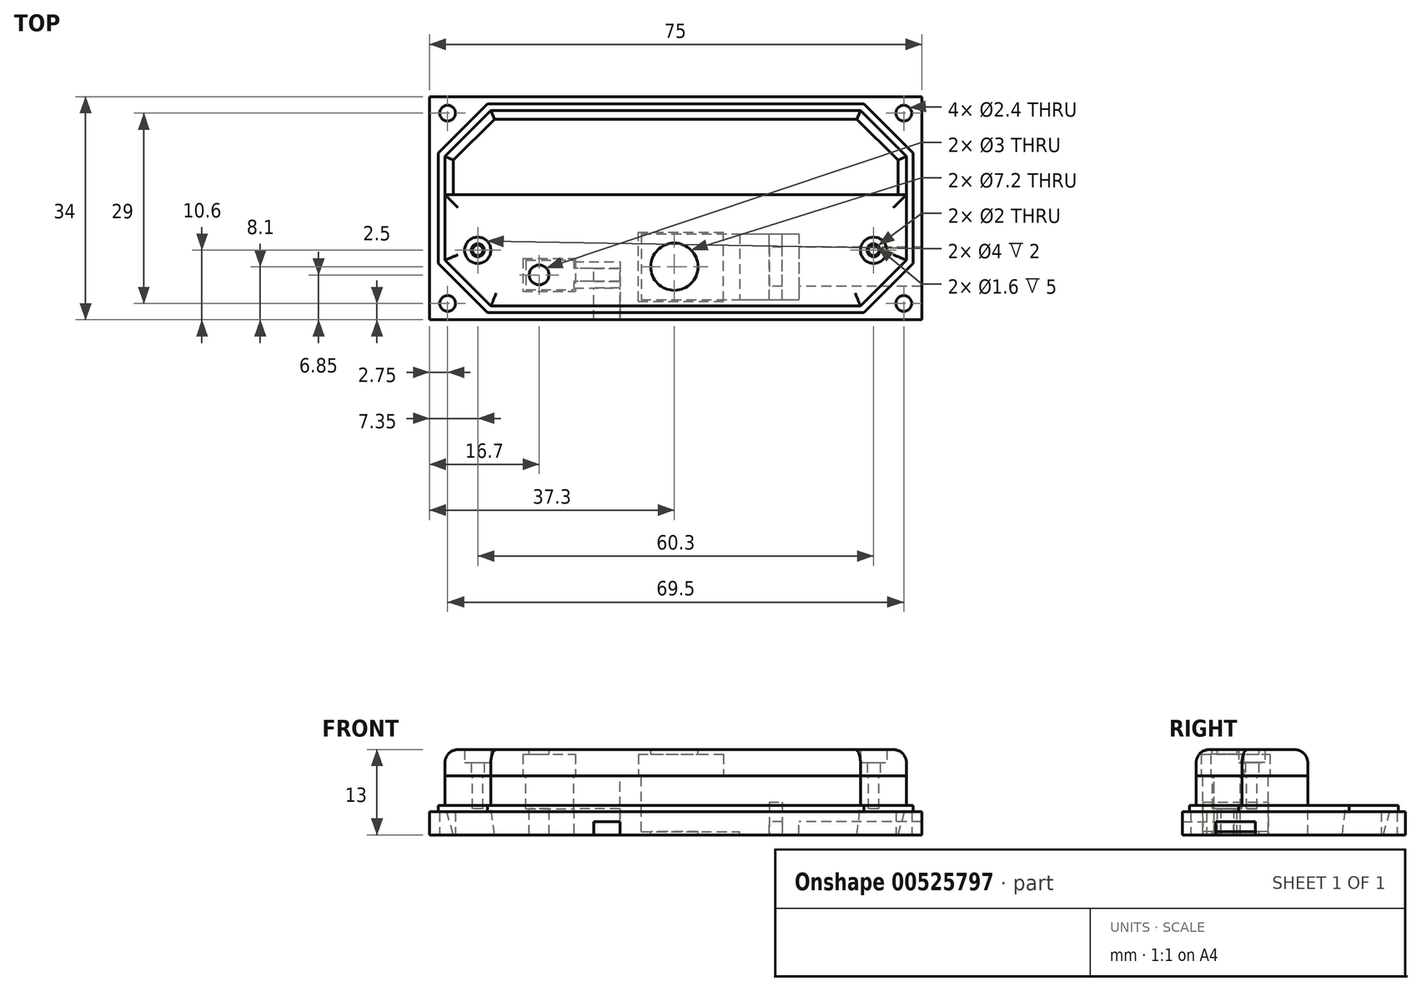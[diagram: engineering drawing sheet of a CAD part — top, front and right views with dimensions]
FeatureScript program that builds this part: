
annotation { "Feature Type Name" : "Feature", "Feature Type Description" : "" }
export const myFeature = defineFeature(function(context is Context, id is Id, definition is map)
    precondition{}
    {
        {
            var Q0;
            Q0=qCreatedBy(makeId("Top.planeOp"),FACE);
            var sketch = newSketch(context, id + "F0", { "sketchPlane" : qUnion([Q0])});
            skLineSegment(sketch, "E0.bottom", {"start": v(37.5, -17) * mm, "end": v(-37.5, -17) * mm});
            skLineSegment(sketch, "E0.top", {"start": v(37.5, 17) * mm, "end": v(-37.5, 17) * mm});
            skLineSegment(sketch, "E0.left", {"start": v(37.5, -17) * mm, "end": v(37.5, 17) * mm});
            skLineSegment(sketch, "E0.right", {"start": v(-37.5, -17) * mm, "end": v(-37.5, 17) * mm});
            skPoint(sketch, "E0.middle", {"position": v(0, 0) * mm});
            skLineSegment(sketch, "E1.bottom", {"start": v(-28.65, 15.9) * mm, "end": v(28.65, 15.9) * mm, "construction": true});
            skLineSegment(sketch, "E1.top", {"start": v(-28.65, -15.9) * mm, "end": v(28.65, -15.9) * mm, "construction": true});
            skLineSegment(sketch, "E1.left", {"start": v(-36.15, 8.4) * mm, "end": v(-36.15, -8.4) * mm, "construction": true});
            skLineSegment(sketch, "E1.right", {"start": v(36.15, 8.4) * mm, "end": v(36.15, -8.4) * mm, "construction": true});
            skLineSegment(sketch, "E2", {"start": v(-36.15, 8.4) * mm, "end": v(-28.65, 15.9) * mm, "construction": true});
            skLineSegment(sketch, "E3", {"start": v(28.65, 15.9) * mm, "end": v(36.15, 8.4) * mm, "construction": true});
            skLineSegment(sketch, "E4", {"start": v(36.15, -8.4) * mm, "end": v(28.65, -15.9) * mm, "construction": true});
            skLineSegment(sketch, "E5", {"start": v(-36.15, -8.4) * mm, "end": v(-28.65, -15.9) * mm, "construction": true});
            skCircle(sketch, "E6", {"center": v(-34.75, 14.5) * mm, "radius": 1.2 * mm});
            skCircle(sketch, "E7", {"center": v(34.75, 14.5) * mm, "radius": 1.2 * mm});
            skCircle(sketch, "E8", {"center": v(-34.75, -14.5) * mm, "radius": 1.2 * mm});
            skCircle(sketch, "E9", {"center": v(34.75, -14.5) * mm, "radius": 1.2 * mm});
            skLineSegment(sketch, "E10", {"start": v(0, -47.1) * mm, "end": v(0, -78.86) * mm, "construction": true});
            skSolve(sketch);
        }
        {
            var Q0;
            Q0=qSketchRegion(id+"F0",true);
            extrude(context, id + "F1", {"entities" : qUnion([Q0]), "depth" : 3.5 * mm});
        }
        {
            var Q0;
            Q0=makeQuery(id+"F1.opExtrude","CAP_FACE",FACE,{"disambiguationData":[OSD([sQuery(id+"F0.wireOp",EDGE,"E0.bottom"),sQuery(id+"F0.wireOp",EDGE,"E0.top"),sQuery(id+"F0.wireOp",EDGE,"E0.left"),sQuery(id+"F0.wireOp",EDGE,"E0.right"),sQuery(id+"F0.wireOp",EDGE,"E6"),sQuery(id+"F0.wireOp",EDGE,"E7"),sQuery(id+"F0.wireOp",EDGE,"E8"),sQuery(id+"F0.wireOp",EDGE,"E9")])],"isStart":false});
            var sketch = newSketch(context, id + "F2", { "sketchPlane" : qUnion([Q0])});
            skLineSegment(sketch, "E11.bottom", {"start": v(-28.65, 15.9) * mm, "end": v(28.65, 15.9) * mm});
            skLineSegment(sketch, "E11.top", {"start": v(-28.65, -15.9) * mm, "end": v(28.65, -15.9) * mm});
            skLineSegment(sketch, "E11.left", {"start": v(-36.15, 8.4) * mm, "end": v(-36.15, -8.4) * mm});
            skLineSegment(sketch, "E11.right", {"start": v(36.15, 8.4) * mm, "end": v(36.15, -8.4) * mm});
            skLineSegment(sketch, "E12", {"start": v(-36.15, 8.4) * mm, "end": v(-28.65, 15.9) * mm});
            skLineSegment(sketch, "E13", {"start": v(28.65, 15.9) * mm, "end": v(36.15, 8.4) * mm});
            skLineSegment(sketch, "E14", {"start": v(36.15, -8.4) * mm, "end": v(28.65, -15.9) * mm});
            skLineSegment(sketch, "E15", {"start": v(-36.15, -8.4) * mm, "end": v(-28.65, -15.9) * mm});
            skSolve(sketch);
        }
        {
            var Q0;
            Q0=qSketchRegion(id+"F2",true);
            extrude(context, id + "F3", {"entities" : qUnion([Q0]), "operationType" : NewBodyOperationType.ADD, "depth" : 1 * mm});
        }
        {
            var Q0;
            Q0=makeQuery(id+"F3.opExtrude","CAP_FACE",FACE,{"disambiguationData":[OSD([sQuery(id+"F2.wireOp",EDGE,"E11.bottom"),sQuery(id+"F2.wireOp",EDGE,"E11.top"),sQuery(id+"F2.wireOp",EDGE,"E11.left"),sQuery(id+"F2.wireOp",EDGE,"E11.right"),sQuery(id+"F2.wireOp",EDGE,"E12"),sQuery(id+"F2.wireOp",EDGE,"E13"),sQuery(id+"F2.wireOp",EDGE,"E14"),sQuery(id+"F2.wireOp",EDGE,"E15")])],"isStart":false});
            var sketch = newSketch(context, id + "F4", { "sketchPlane" : qUnion([Q0])});
            skLineSegment(sketch, "E16.bottom", {"start": v(-28.15, 14.9) * mm, "end": v(28.15, 14.9) * mm});
            skLineSegment(sketch, "E16.top", {"start": v(-28.15, -14.9) * mm, "end": v(28.15, -14.9) * mm});
            skLineSegment(sketch, "E16.left", {"start": v(-35.15, 7.9) * mm, "end": v(-35.15, -7.9) * mm});
            skLineSegment(sketch, "E16.right", {"start": v(35.15, 7.9) * mm, "end": v(35.15, -7.9) * mm});
            skLineSegment(sketch, "E17", {"start": v(-35.15, 7.9) * mm, "end": v(-28.15, 14.9) * mm});
            skLineSegment(sketch, "E18", {"start": v(28.15, 14.9) * mm, "end": v(35.15, 7.9) * mm});
            skLineSegment(sketch, "E19", {"start": v(35.15, -7.9) * mm, "end": v(28.15, -14.9) * mm});
            skLineSegment(sketch, "E20", {"start": v(-35.15, -7.9) * mm, "end": v(-28.15, -14.9) * mm});
            skSolve(sketch);
        }
        {
            var Q0;
            Q0=qSketchRegion(id+"F4",true);
            extrude(context, id + "F5", {"entities" : qUnion([Q0]), "operationType" : NewBodyOperationType.REMOVE, "oppositeDirection" : true, "depth" : 5 * mm});
        }
        {
            var Q0;
            Q0=qCreatedBy(makeId("Front.planeOp"),FACE);
            cPlane(context, id + "F6", {"entities" : qUnion([Q0]), "cplaneType" : CPlaneType.OFFSET, "offset" : 2.1 * mm, "oppositeDirection" : true, "width" : 150 * mm, "height" : 150 * mm});
        }
        {
            var Q0;
            Q0=qCreatedBy(id+"F6.planeOp",FACE);
            var sketch = newSketch(context, id + "F7", { "sketchPlane" : qUnion([Q0])});
            skLineSegment(sketch, "E21", {"start": v(-35.15, 4.5) * mm, "end": v(-35.15, 0) * mm});
            skLineSegment(sketch, "E22", {"start": v(-33.85, 0) * mm, "end": v(-35.15, 0) * mm});
            skLineSegment(sketch, "E23", {"start": v(-33.85, 0) * mm, "end": v(-35.15, 4.5) * mm});
            skSolve(sketch);
        }
        {
            var Q0;
            Q0=makeQuery(id+"F3.opExtrude","CAP_FACE",FACE,{"disambiguationData":[OSD([sQuery(id+"F2.wireOp",EDGE,"E11.bottom"),sQuery(id+"F2.wireOp",EDGE,"E11.top"),sQuery(id+"F2.wireOp",EDGE,"E11.left"),sQuery(id+"F2.wireOp",EDGE,"E11.right"),sQuery(id+"F2.wireOp",EDGE,"E12"),sQuery(id+"F2.wireOp",EDGE,"E13"),sQuery(id+"F2.wireOp",EDGE,"E14"),sQuery(id+"F2.wireOp",EDGE,"E15")])],"isStart":false});
            var sketch = newSketch(context, id + "F8", { "sketchPlane" : qUnion([Q0])});
            skLineSegment(sketch, "E24.bottom", {"start": v(-28.15, 14.9) * mm, "end": v(28.15, 14.9) * mm});
            skLineSegment(sketch, "E24.left", {"start": v(-35.15, 7.9) * mm, "end": v(-35.15, 2.1) * mm});
            skLineSegment(sketch, "E24.right", {"start": v(35.15, 7.9) * mm, "end": v(35.15, 2.1) * mm});
            skLineSegment(sketch, "E25", {"start": v(-35.15, 7.9) * mm, "end": v(-28.15, 14.9) * mm});
            skLineSegment(sketch, "E26", {"start": v(28.15, 14.9) * mm, "end": v(35.15, 7.9) * mm});
            skSolve(sketch);
        }
        {
            var Q0;
            Q0=qSketchRegion(id+"F7",true);
            var Q1;
            Q1=qConstructionFilter(qBodyType(qCreatedBy(id+"F8",EDGE),BodyType.WIRE),ConstructionObject.NO);
            sweep(context, id + "F9", {"operationType" : NewBodyOperationType.ADD, "profiles" : qUnion([Q0]), "path" : qUnion([Q1])});
        }
        {
            var Q0;
            Q0=qCreatedBy(makeId("Top.planeOp"),FACE);
            var sketch = newSketch(context, id + "F10", { "sketchPlane" : qUnion([Q0])});
            skLineSegment(sketch, "E27.top", {"start": v(-28.15, -14.9) * mm, "end": v(28.15, -14.9) * mm});
            skLineSegment(sketch, "E27.left", {"start": v(-35.15, 2.1) * mm, "end": v(-35.15, -7.9) * mm});
            skLineSegment(sketch, "E27.right", {"start": v(35.15, 2.1) * mm, "end": v(35.15, -7.9) * mm});
            skLineSegment(sketch, "E28", {"start": v(35.15, -7.9) * mm, "end": v(28.15, -14.9) * mm});
            skLineSegment(sketch, "E29", {"start": v(-35.15, -7.9) * mm, "end": v(-28.15, -14.9) * mm});
            skLineSegment(sketch, "E30", {"start": v(-35.15, 2.1) * mm, "end": v(35.15, 2.1) * mm});
            skSolve(sketch);
        }
        {
            var Q0;
            Q0=qSketchRegion(id+"F10",true);
            extrude(context, id + "F11", {"entities" : qUnion([Q0]), "operationType" : NewBodyOperationType.ADD, "depth" : 9 * mm});
        }
        {
            var Q0;
            Q0=makeQuery(id+"F11.opExtrude","CAP_FACE",FACE,{"disambiguationData":[OSD([sQuery(id+"F10.wireOp",EDGE,"E27.top"),sQuery(id+"F10.wireOp",EDGE,"E27.left"),sQuery(id+"F10.wireOp",EDGE,"E27.right"),sQuery(id+"F10.wireOp",EDGE,"E28"),sQuery(id+"F10.wireOp",EDGE,"E29"),sQuery(id+"F10.wireOp",EDGE,"E30")])],"isStart":false});
            var sketch = newSketch(context, id + "F12", { "sketchPlane" : qUnion([Q0])});
            skLineSegment(sketch, "E31.bottom", {"start": v(-5.25, -3.9) * mm, "end": v(9.75, -3.9) * mm});
            skLineSegment(sketch, "E31.top", {"start": v(-5.25, -13.9) * mm, "end": v(9.75, -13.9) * mm});
            skLineSegment(sketch, "E31.left", {"start": v(-5.25, -3.9) * mm, "end": v(-5.25, -13.9) * mm});
            skLineSegment(sketch, "E31.right", {"start": v(9.75, -3.9) * mm, "end": v(9.75, -13.9) * mm});
            skSolve(sketch);
        }
        {
            var Q0;
            Q0=qSketchRegion(id+"F12",true);
            extrude(context, id + "F13", {"entities" : qUnion([Q0]), "operationType" : NewBodyOperationType.REMOVE, "oppositeDirection" : true, "depth" : 8.5 * mm});
        }
        {
            var Q0;
            Q0=makeQuery(id+"F11.opExtrude","CAP_FACE",FACE,{"disambiguationData":[OSD([sQuery(id+"F10.wireOp",EDGE,"E27.top"),sQuery(id+"F10.wireOp",EDGE,"E27.left"),sQuery(id+"F10.wireOp",EDGE,"E27.right"),sQuery(id+"F10.wireOp",EDGE,"E28"),sQuery(id+"F10.wireOp",EDGE,"E29"),sQuery(id+"F10.wireOp",EDGE,"E30")])],"isStart":false});
            var sketch = newSketch(context, id + "F14", { "sketchPlane" : qUnion([Q0])});
            skLineSegment(sketch, "E32.bottom", {"start": v(-22.8, -7.9) * mm, "end": v(-15.5, -7.9) * mm});
            skLineSegment(sketch, "E32.top", {"start": v(-22.8, -12.4) * mm, "end": v(-15.5, -12.4) * mm});
            skLineSegment(sketch, "E32.left", {"start": v(-22.8, -7.9) * mm, "end": v(-22.8, -12.4) * mm});
            skLineSegment(sketch, "E32.right", {"start": v(-15.5, -7.9) * mm, "end": v(-15.5, -12.4) * mm});
            skSolve(sketch);
        }
        {
            var Q0;
            Q0=qSketchRegion(id+"F14",true);
            extrude(context, id + "F15", {"entities" : qUnion([Q0]), "operationType" : NewBodyOperationType.REMOVE, "oppositeDirection" : true, "depth" : 5 * mm});
        }
        {
            var Q0;
            Q0=makeQuery(id+"F11.opExtrude","CAP_FACE",FACE,{"disambiguationData":[OSD([sQuery(id+"F10.wireOp",EDGE,"E27.top"),sQuery(id+"F10.wireOp",EDGE,"E27.left"),sQuery(id+"F10.wireOp",EDGE,"E27.right"),sQuery(id+"F10.wireOp",EDGE,"E28"),sQuery(id+"F10.wireOp",EDGE,"E29"),sQuery(id+"F10.wireOp",EDGE,"E30")])],"isStart":false});
            var sketch = newSketch(context, id + "F16", { "sketchPlane" : qUnion([Q0])});
            skLineSegment(sketch, "E33.bottom", {"start": v(9.75, -3.9) * mm, "end": v(18.75, -3.9) * mm});
            skLineSegment(sketch, "E33.top", {"start": v(9.75, -13.9) * mm, "end": v(18.75, -13.9) * mm});
            skLineSegment(sketch, "E33.left", {"start": v(9.75, -3.9) * mm, "end": v(9.75, -13.9) * mm});
            skLineSegment(sketch, "E33.right", {"start": v(18.75, -3.9) * mm, "end": v(18.75, -13.9) * mm});
            skLineSegment(sketch, "E34.bottom", {"start": v(-15.5, -8.15) * mm, "end": v(-8.5, -8.15) * mm});
            skLineSegment(sketch, "E34.top", {"start": v(-15.5, -12.15) * mm, "end": v(-8.5, -12.15) * mm});
            skLineSegment(sketch, "E34.left", {"start": v(-15.5, -8.15) * mm, "end": v(-15.5, -12.15) * mm});
            skLineSegment(sketch, "E34.right", {"start": v(-8.5, -8.15) * mm, "end": v(-8.5, -12.15) * mm});
            skSolve(sketch);
        }
        {
            var Q0;
            Q0=qSketchRegion(id+"F16",true);
            extrude(context, id + "F17", {"entities" : qUnion([Q0]), "operationType" : NewBodyOperationType.REMOVE, "oppositeDirection" : true, "depth" : 25 * mm});
        }
        {
            var Q0;
            Q0=makeQuery(id+"F17.boolean.opBoolean","MERGE",FACE,{"derivedFrom":[makeQuery(id+"F13.boolean.opBoolean","COPY",FACE,{"derivedFrom":makeQuery(id+"F13.opExtrude","SWEPT_FACE",FACE,{"disambiguationData":[OSD([sQuery(id+"F12.wireOp",EDGE,"E31.bottom")])]})}),makeQuery(id+"F17.opExtrude","SWEPT_FACE",FACE,{"disambiguationData":[OSD([sQuery(id+"F16.wireOp",EDGE,"E33.bottom")])]})]});
            var sketch = newSketch(context, id + "F18", { "sketchPlane" : qUnion([Q0])});
            skLineSegment(sketch, "E35.bottom", {"start": v(14.25, 5) * mm, "end": v(16.25, 5) * mm});
            skLineSegment(sketch, "E35.top", {"start": v(14.25, 0) * mm, "end": v(16.25, 0) * mm});
            skLineSegment(sketch, "E35.left", {"start": v(14.25, 5) * mm, "end": v(14.25, 0) * mm});
            skLineSegment(sketch, "E35.right", {"start": v(16.25, 5) * mm, "end": v(16.25, 0) * mm});
            skSolve(sketch);
        }
        {
            var Q0;
            Q0=qSketchRegion(id+"F18",true);
            extrude(context, id + "F19", {"entities" : qUnion([Q0]), "operationType" : NewBodyOperationType.ADD, "depth" : 10 * mm});
        }
        {
            var Q0;
            Q0=makeQuery(id+"F19.opExtrude","SWEPT_FACE",FACE,{"disambiguationData":[OSD([sQuery(id+"F18.wireOp",EDGE,"E35.left")])]});
            var sketch = newSketch(context, id + "F20", { "sketchPlane" : qUnion([Q0])});
            skLineSegment(sketch, "E36.bottom", {"start": v(5.9, 0) * mm, "end": v(11.9, 0) * mm});
            skLineSegment(sketch, "E36.top", {"start": v(5.9, 2) * mm, "end": v(11.9, 2) * mm});
            skLineSegment(sketch, "E36.left", {"start": v(5.9, 0) * mm, "end": v(5.9, 2) * mm});
            skLineSegment(sketch, "E36.right", {"start": v(11.9, 0) * mm, "end": v(11.9, 2) * mm});
            skSolve(sketch);
        }
        {
            var Q0;
            Q0=qSketchRegion(id+"F20",true);
            extrude(context, id + "F21", {"entities" : qUnion([Q0]), "operationType" : NewBodyOperationType.REMOVE, "oppositeDirection" : true, "depth" : 25 * mm});
        }
        {
            var Q0;
            Q0=makeQuery(id+"F11.opExtrude","CAP_FACE",FACE,{"disambiguationData":[OSD([sQuery(id+"F10.wireOp",EDGE,"E27.top"),sQuery(id+"F10.wireOp",EDGE,"E27.left"),sQuery(id+"F10.wireOp",EDGE,"E27.right"),sQuery(id+"F10.wireOp",EDGE,"E28"),sQuery(id+"F10.wireOp",EDGE,"E29"),sQuery(id+"F10.wireOp",EDGE,"E30")])],"isStart":false});
            var sketch = newSketch(context, id + "F22", { "sketchPlane" : qUnion([Q0])});
            skCircle(sketch, "E37", {"center": v(-30.15, -6.4) * mm, "radius": 0.8 * mm});
            skCircle(sketch, "E38", {"center": v(30.15, -6.4) * mm, "radius": 0.8 * mm});
            skSolve(sketch);
        }
        {
            var Q0;
            Q0=qSketchRegion(id+"F22",true);
            extrude(context, id + "F23", {"entities" : qUnion([Q0]), "operationType" : NewBodyOperationType.REMOVE, "oppositeDirection" : true, "depth" : 5 * mm});
        }
        {
            var Q0;
            Q0=qCreatedBy(makeId("Top.planeOp"),FACE);
            cPlane(context, id + "F24", {"entities" : qUnion([Q0]), "cplaneType" : CPlaneType.OFFSET, "offset" : 9 * mm, "width" : 150 * mm, "height" : 150 * mm});
        }
        {
            var Q0;
            Q0=qCreatedBy(id+"F24.planeOp",FACE);
            var sketch = newSketch(context, id + "F25", { "sketchPlane" : qUnion([Q0])});
            skLineSegment(sketch, "E39.top", {"start": v(-28.15, -14.9) * mm, "end": v(28.15, -14.9) * mm});
            skLineSegment(sketch, "E39.left", {"start": v(-35.15, 2.1) * mm, "end": v(-35.15, -7.9) * mm});
            skLineSegment(sketch, "E39.right", {"start": v(35.15, 2.1) * mm, "end": v(35.15, -7.9) * mm});
            skLineSegment(sketch, "E40", {"start": v(35.15, -7.9) * mm, "end": v(28.15, -14.9) * mm});
            skLineSegment(sketch, "E41", {"start": v(-35.15, -7.9) * mm, "end": v(-28.15, -14.9) * mm});
            skLineSegment(sketch, "E42", {"start": v(-35.15, 2.1) * mm, "end": v(35.15, 2.1) * mm});
            skSolve(sketch);
        }
        {
            var Q0;
            Q0=qSketchRegion(id+"F25",true);
            extrude(context, id + "F26", {"entities" : qUnion([Q0]), "depth" : 4 * mm});
        }
        {
            var Q0;
            Q0=makeQuery(id+"F26.opExtrude","CAP_FACE",FACE,{"disambiguationData":[OSD([sQuery(id+"F25.wireOp",EDGE,"E39.top"),sQuery(id+"F25.wireOp",EDGE,"E39.left"),sQuery(id+"F25.wireOp",EDGE,"E39.right"),sQuery(id+"F25.wireOp",EDGE,"E40"),sQuery(id+"F25.wireOp",EDGE,"E41"),sQuery(id+"F25.wireOp",EDGE,"E42")])],"isStart":false});
            var sketch = newSketch(context, id + "F27", { "sketchPlane" : qUnion([Q0])});
            skCircle(sketch, "E43", {"center": v(-0.2, -8.9) * mm, "radius": 3.6 * mm});
            skCircle(sketch, "E44", {"center": v(-20.8, -10.15) * mm, "radius": 1.5 * mm});
            skSolve(sketch);
        }
        {
            var Q0;
            Q0=qSketchRegion(id+"F27",true);
            extrude(context, id + "F28", {"entities" : qUnion([Q0]), "operationType" : NewBodyOperationType.REMOVE, "oppositeDirection" : true, "depth" : 25 * mm});
        }
        {
            var Q0;
            Q0=makeQuery(id+"F26.opExtrude","CAP_FACE",FACE,{"disambiguationData":[OSD([sQuery(id+"F25.wireOp",EDGE,"E39.top"),sQuery(id+"F25.wireOp",EDGE,"E39.left"),sQuery(id+"F25.wireOp",EDGE,"E39.right"),sQuery(id+"F25.wireOp",EDGE,"E40"),sQuery(id+"F25.wireOp",EDGE,"E41"),sQuery(id+"F25.wireOp",EDGE,"E42")])],"isStart":true});
            var sketch = newSketch(context, id + "F29", { "sketchPlane" : qUnion([Q0])});
            skLineSegment(sketch, "E45.bottom", {"start": v(-5.7, 14.15) * mm, "end": v(7.3, 14.15) * mm});
            skLineSegment(sketch, "E45.top", {"start": v(-5.7, 3.65) * mm, "end": v(7.3, 3.65) * mm});
            skLineSegment(sketch, "E45.left", {"start": v(-5.7, 14.15) * mm, "end": v(-5.7, 3.65) * mm});
            skLineSegment(sketch, "E45.right", {"start": v(7.3, 14.15) * mm, "end": v(7.3, 3.65) * mm});
            skPoint(sketch, "E45.middle", {"position": v(0.8, 8.9) * mm});
            skLineSegment(sketch, "E46.bottom", {"start": v(-23.3, 7.65) * mm, "end": v(-15.3, 7.65) * mm});
            skLineSegment(sketch, "E46.top", {"start": v(-23.3, 12.65) * mm, "end": v(-15.3, 12.65) * mm});
            skLineSegment(sketch, "E46.left", {"start": v(-23.3, 7.65) * mm, "end": v(-23.3, 12.65) * mm});
            skLineSegment(sketch, "E46.right", {"start": v(-15.3, 7.65) * mm, "end": v(-15.3, 12.65) * mm});
            skCircle(sketch, "E47", {"center": v(-20.8, 10.15) * mm, "radius": 1.5 * mm, "construction": true});
            skSolve(sketch);
        }
        {
            var Q0;
            Q0=qSketchRegion(id+"F29",true);
            extrude(context, id + "F30", {"entities" : qUnion([Q0]), "operationType" : NewBodyOperationType.REMOVE, "oppositeDirection" : true, "depth" : 3.3 * mm});
        }
        {
            var Q0;
            Q0=makeQuery(id+"F17.boolean.opBoolean","COPY",FACE,{"derivedFrom":makeQuery(id+"F17.opExtrude","SWEPT_FACE",FACE,{"disambiguationData":[OSD([sQuery(id+"F16.wireOp",EDGE,"E34.left")])]})});
            var sketch = newSketch(context, id + "F31", { "sketchPlane" : qUnion([Q0])});
            skLineSegment(sketch, "E48.bottom", {"start": v(-11.15, 4) * mm, "end": v(-9.15, 4) * mm});
            skLineSegment(sketch, "E48.top", {"start": v(-11.15, 0) * mm, "end": v(-9.15, 0) * mm});
            skLineSegment(sketch, "E48.left", {"start": v(-11.15, 4) * mm, "end": v(-11.15, 0) * mm});
            skLineSegment(sketch, "E48.right", {"start": v(-9.15, 4) * mm, "end": v(-9.15, 0) * mm});
            skSolve(sketch);
        }
        {
            var Q0;
            Q0=qSketchRegion(id+"F31",true);
            extrude(context, id + "F32", {"entities" : qUnion([Q0]), "operationType" : NewBodyOperationType.ADD, "depth" : 7 * mm});
        }
        {
            var Q0;
            Q0=makeQuery(id+"F32.opExtrude","SWEPT_FACE",FACE,{"disambiguationData":[OSD([sQuery(id+"F31.wireOp",EDGE,"E48.right")])]});
            var sketch = newSketch(context, id + "F33", { "sketchPlane" : qUnion([Q0])});
            skLineSegment(sketch, "E49.bottom", {"start": v(12.5, 0) * mm, "end": v(8.5, 0) * mm});
            skLineSegment(sketch, "E49.top", {"start": v(12.5, 2) * mm, "end": v(8.5, 2) * mm});
            skLineSegment(sketch, "E49.left", {"start": v(12.5, 0) * mm, "end": v(12.5, 2) * mm});
            skLineSegment(sketch, "E49.right", {"start": v(8.5, 0) * mm, "end": v(8.5, 2) * mm});
            skSolve(sketch);
        }
        {
            var Q0;
            Q0=qSketchRegion(id+"F33",true);
            extrude(context, id + "F34", {"entities" : qUnion([Q0]), "operationType" : NewBodyOperationType.REMOVE, "oppositeDirection" : true, "depth" : 25 * mm});
        }
        {
            var Q0;
            Q0=makeQuery(id+"F26.opExtrude","CAP_FACE",FACE,{"disambiguationData":[OSD([sQuery(id+"F25.wireOp",EDGE,"E39.top"),sQuery(id+"F25.wireOp",EDGE,"E39.left"),sQuery(id+"F25.wireOp",EDGE,"E39.right"),sQuery(id+"F25.wireOp",EDGE,"E40"),sQuery(id+"F25.wireOp",EDGE,"E41"),sQuery(id+"F25.wireOp",EDGE,"E42")])],"isStart":false});
            var sketch = newSketch(context, id + "F35", { "sketchPlane" : qUnion([Q0])});
            skCircle(sketch, "E50", {"center": v(-30.15, -6.4) * mm, "radius": 1 * mm, "construction": true});
            skCircle(sketch, "E51", {"center": v(30.15, -6.4) * mm, "radius": 1 * mm, "construction": true});
            skSolve(sketch);
        }
        {
            var Q0;
            Q0=sQuery(id+"F35.wireOp",VERTEX,"E50.center");
            var Q1;
            Q1=sQuery(id+"F35.wireOp",VERTEX,"E51.center");
            var Q2;
            Q2=makeQuery(id+"F26.opExtrude","SWEPT_BODY",BODY,{"disambiguationData":[OSD([sQuery(id+"F25.wireOp",EDGE,"E39.top"),sQuery(id+"F25.wireOp",EDGE,"E39.left"),sQuery(id+"F25.wireOp",EDGE,"E39.right"),sQuery(id+"F25.wireOp",EDGE,"E40"),sQuery(id+"F25.wireOp",EDGE,"E41"),sQuery(id+"F25.wireOp",EDGE,"E42")])]});
            hole(context, id + "F36", {"style" : HoleStyle.C_BORE, "endStyle" : HoleEndStyle.BLIND, "holeDiameter" : 2 * mm, "cBoreDiameter" : 4 * mm, "cBoreDepth" : 2 * mm, "holeDepth" : 10 * mm, "tappedDepth" : 12 * mm, "tapClearance" : 3, "locations" : qUnion([Q0, Q1]), "scope" : qUnion([Q2])});
        }
        {
            var Q0;
            Q0=makeQuery(id+"F26.opExtrude","CAP_EDGE",EDGE,{"disambiguationData":[OSD([sQuery(id+"F25.wireOp",EDGE,"E39.top")])],"isStart":false});
            var Q1;
            Q1=makeQuery(id+"F26.opExtrude","CAP_EDGE",EDGE,{"disambiguationData":[OSD([sQuery(id+"F25.wireOp",EDGE,"E41")])],"isStart":false});
            var Q2;
            Q2=makeQuery(id+"F26.opExtrude","CAP_EDGE",EDGE,{"disambiguationData":[OSD([sQuery(id+"F25.wireOp",EDGE,"E39.left")])],"isStart":false});
            var Q3;
            Q3=makeQuery(id+"F26.opExtrude","CAP_EDGE",EDGE,{"disambiguationData":[OSD([sQuery(id+"F25.wireOp",EDGE,"E42")])],"isStart":false});
            var Q4;
            Q4=makeQuery(id+"F26.opExtrude","CAP_EDGE",EDGE,{"disambiguationData":[OSD([sQuery(id+"F25.wireOp",EDGE,"E39.right")])],"isStart":false});
            var Q5;
            Q5=makeQuery(id+"F26.opExtrude","CAP_EDGE",EDGE,{"disambiguationData":[OSD([sQuery(id+"F25.wireOp",EDGE,"E40")])],"isStart":false});
            fillet(context, id + "F37", {"entities" : qUnion([Q0, Q1, Q2, Q3, Q4, Q5]), "radius" : 2 * mm, "tangentPropagation" : true, "allowEdgeOverflow" : false});
        }
    });
